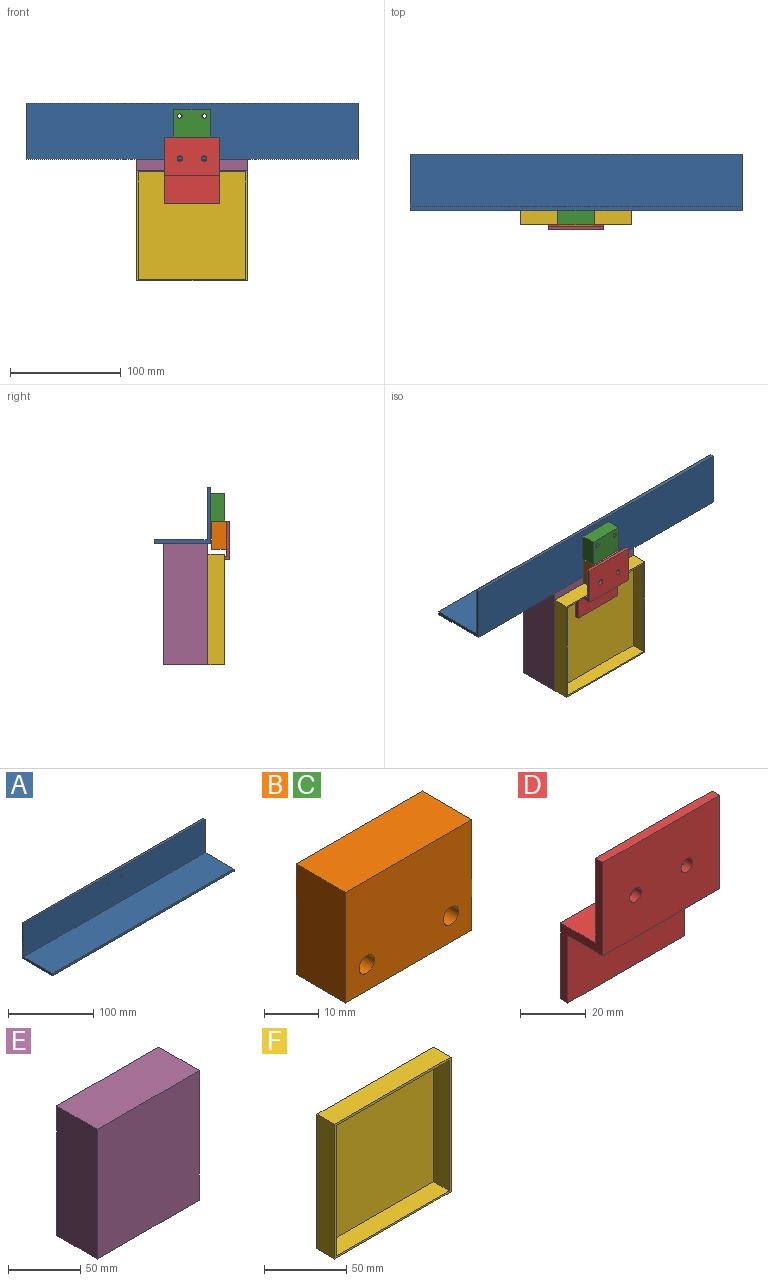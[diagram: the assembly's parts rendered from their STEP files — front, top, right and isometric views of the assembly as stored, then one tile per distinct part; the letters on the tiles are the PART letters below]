
ASSEMBLY  parts=6 mates=4
PART A: 10 faces, bbox 300x50.8x50.8 mm
  f0: plane 300x50.8mm, normal (0,0,-1), area 15240mm2, adj f1,f5,f6,f7
  f1: plane 300x50.8mm, normal (0,1,0), area 15214.9mm2, adj f0,f2,f6,f7,f8,f9
  f2: plane 300x3.18mm, normal (0,0,1), area 952.5mm2, adj f1,f3,f6,f7
  f3: plane 300x47.63mm, normal (0,-1,0), area 14262.4mm2, adj f2,f4,f6,f7,f8,f9
  f4: plane 300x47.63mm, normal (0,0,1), area 14287.5mm2, adj f3,f5,f6,f7
  f5: plane 300x3.18mm, normal (0,-1,0), area 952.5mm2, adj f0,f4,f6,f7
  f6: plane 50.8x50.8mm, normal (1,0,0), area 312.5mm2, adj f0,f1,f2,f3,f4,f5
  f7: plane 50.8x50.8mm, normal (-1,0,0), area 312.5mm2, adj f0,f1,f2,f3,f4,f5
  f8: cylinder r=2mm len=4mm, axis (0,1,0), area 39.9mm2, adj f1,f3
  f9: cylinder r=2mm len=4mm, axis (0,1,0), area 39.9mm2, adj f1,f3
PART B: 8 faces, bbox 33x13x25 mm
  f0: plane 33x13mm, normal (0,0,-1), area 429mm2, adj f1,f3,f6,f7
  f1: plane 25x13mm, normal (1,0,0), area 325mm2, adj f0,f2,f6,f7
  f2: plane 33x13mm, normal (0,0,1), area 429mm2, adj f1,f3,f6,f7
  f3: plane 25x13mm, normal (-1,0,0), area 325mm2, adj f0,f2,f6,f7
  f4: cylinder r=2mm len=13mm, axis (0,1,0), area 163.4mm2, adj f6,f7
  f5: cylinder r=2mm len=13mm, axis (0,1,0), area 163.4mm2, adj f6,f7
  f6: plane 33x25mm, normal (0,-1,0), area 799.9mm2, adj f0,f1,f2,f3,f4,f5
  f7: plane 33x25mm, normal (0,1,0), area 799.9mm2, adj f0,f1,f2,f3,f4,f5
PART C: same geometry as B
PART D: 12 faces, bbox 50x18.2x59.7 mm
  f0: plane 50x15mm, normal (0,0,-1), area 750mm2, adj f4,f6,f7,f8
  f1: plane 50x15mm, normal (0,0,1), area 750mm2, adj f2,f5,f6,f7
  f2: plane 50x31.5mm, normal (0,1,0), area 1535.7mm2, adj f1,f3,f6,f7,f10,f11
  f3: plane 50x3.18mm, normal (0,0,1), area 158.8mm2, adj f2,f4,f6,f7
  f4: plane 50x34.68mm, normal (0,-1,0), area 1694.5mm2, adj f0,f3,f6,f7,f10,f11
  f5: plane 50x28.18mm, normal (0,1,0), area 1408.8mm2, adj f1,f6,f7,f9
  f6: plane 59.68x18.18mm, normal (1,0,0), area 237.1mm2, adj f0,f1,f2,f3,f4,f5,f8,f9
  f7: plane 59.68x18.18mm, normal (-1,0,0), area 237.1mm2, adj f0,f1,f2,f3,f4,f5,f8,f9
  f8: plane 50x25mm, normal (0,-1,0), area 1250mm2, adj f0,f6,f7,f9
  f9: plane 50x3.18mm, normal (0,0,-1), area 158.7mm2, adj f5,f6,f7,f8
  f10: cylinder r=2.5mm len=5mm, axis (0,1,0), area 49.9mm2, adj f2,f4
  f11: cylinder r=2.5mm len=5mm, axis (0,1,0), area 49.9mm2, adj f2,f4
PART E: 6 faces, bbox 100x40x110 mm
  f0: plane 110x40mm, normal (-1,0,0), area 4400mm2, adj f1,f3,f4,f5
  f1: plane 100x40mm, normal (0,0,-1), area 4000mm2, adj f0,f2,f3,f4
  f2: plane 110x40mm, normal (1,0,0), area 4400mm2, adj f1,f3,f4,f5
  f3: plane 110x100mm, normal (0,1,0), area 11000mm2, adj f0,f1,f2,f5
  f4: plane 110x100mm, normal (0,-1,0), area 11000mm2, adj f0,f1,f2,f5
  f5: plane 100x40mm, normal (0,0,1), area 4000mm2, adj f0,f2,f3,f4
PART F: 11 faces, bbox 100x15x100 mm
  f0: plane 100x100mm, normal (0,-1,0), area 591mm2, adj f1,f2,f3,f4,f6,f7,f8,f9
  f1: plane 100x15mm, normal (0,0,1), area 1500mm2, adj f0,f2,f4,f5
  f2: plane 100x15mm, normal (-1,0,0), area 1500mm2, adj f0,f1,f3,f5
  f3: plane 100x15mm, normal (0,0,-1), area 1500mm2, adj f0,f2,f4,f5
  f4: plane 100x15mm, normal (1,0,0), area 1500mm2, adj f0,f1,f3,f5
  f5: plane 100x100mm, normal (0,1,0), area 10000mm2, adj f1,f2,f3,f4
  f6: plane 97x13.5mm, normal (0,0,-1), area 1309.5mm2, adj f0,f7,f9,f10
  f7: plane 97x13.5mm, normal (1,0,0), area 1309.5mm2, adj f0,f6,f8,f10
  f8: plane 97x13.5mm, normal (0,0,1), area 1309.5mm2, adj f0,f7,f9,f10
  f9: plane 97x13.5mm, normal (-1,0,0), area 1309.5mm2, adj f0,f6,f8,f10
  f10: plane 97x97mm, normal (0,-1,0), area 9409mm2, adj f6,f7,f8,f9
PLACE A rot(axis=(0,0,1),180deg) t=(-1.91,-40.93,196.86)mm
PLACE B t=(-168.41,-42.03,191.45)mm
PLACE C rot(axis=(1,0,0),180deg) t=(-168.41,-53.93,241.94)mm
PLACE D t=(-176.91,-55.03,184.95)mm
PLACE E t=(-162.76,-38.53,134.25)mm fixed
PLACE F t=(-162.76,-38.53,134.25)mm fixed
MATE fastened A.f1 <-> C.f6  axis (0,-1,0) through (-151.91,-40.93,222.24)mm
MATE fastened B.f5 <-> D.f11  axis (0,-1,0) through (-162.91,-55.03,197.45)mm
MATE fastened A.f0 <-> E.f5  axis (0,0,-1) through (-151.91,-15.53,196.86)mm
MATE fastened D.f5 <-> F.f10  axis (0,1,0) through (-151.91,-40.03,170.86)mm
